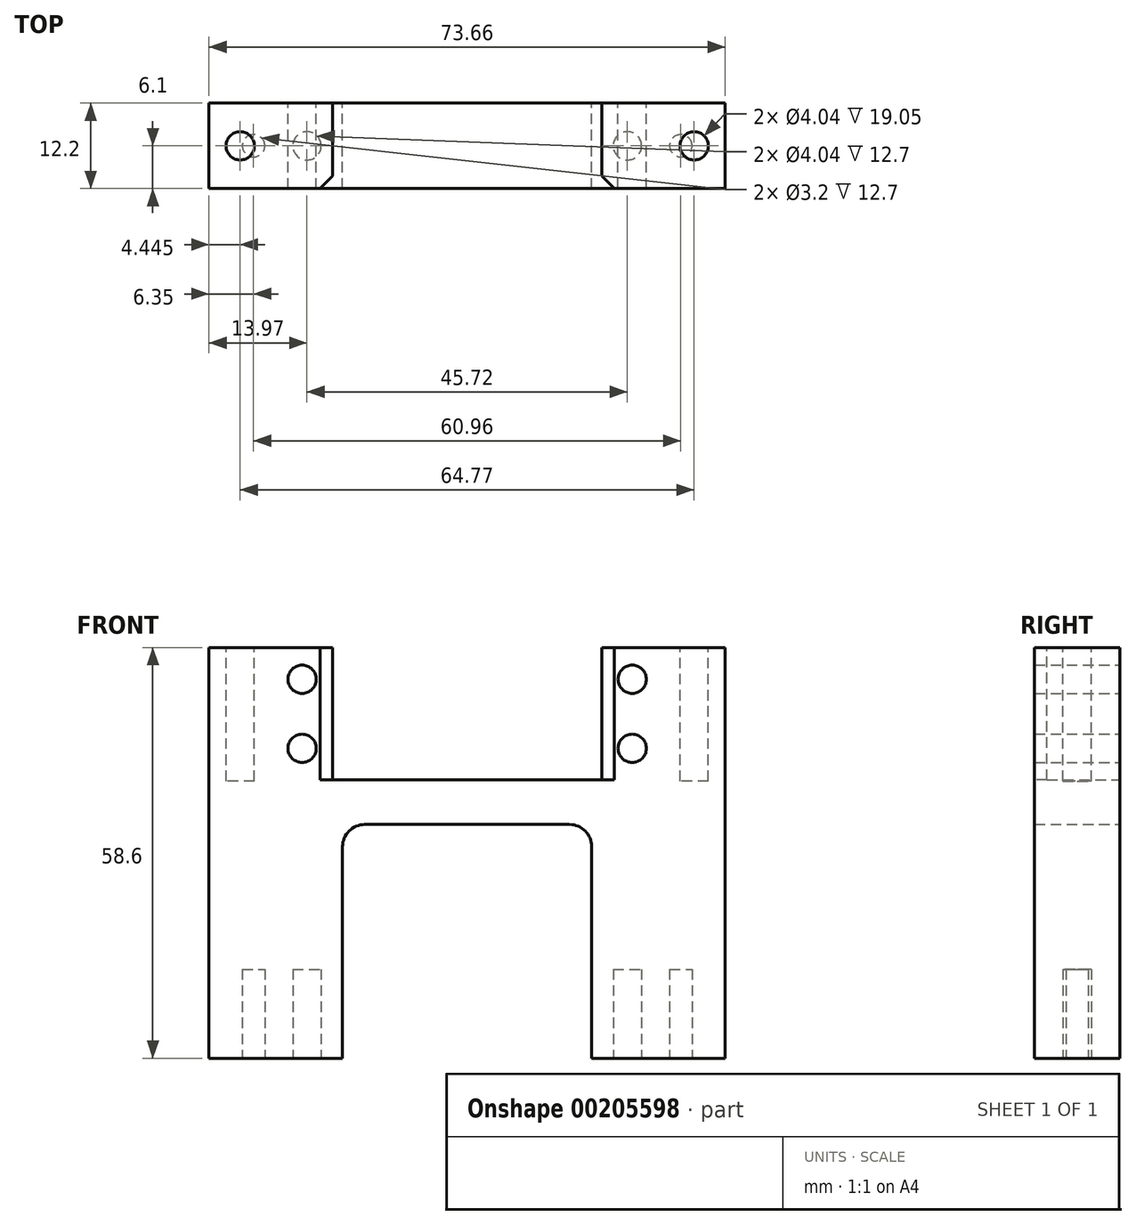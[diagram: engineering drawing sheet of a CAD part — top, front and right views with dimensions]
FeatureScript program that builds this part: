
annotation { "Feature Type Name" : "Feature", "Feature Type Description" : "" }
export const myFeature = defineFeature(function(context is Context, id is Id, definition is map)
    precondition{}
    {
        {
            var Q0;
            Q0=qCreatedBy(makeId("Front.planeOp"),FACE);
            var sketch = newSketch(context, id + "F0", { "sketchPlane" : qUnion([Q0])});
            skLineSegment(sketch, "E0", {"start": v(-36.83, 0) * mm, "end": v(-17.78, 0) * mm});
            skLineSegment(sketch, "E1", {"start": v(36.83, 0) * mm, "end": v(36.83, 58.6) * mm});
            skLineSegment(sketch, "E2", {"start": v(36.83, 58.6) * mm, "end": v(19.2, 58.6) * mm});
            skLineSegment(sketch, "E3", {"start": v(19.2, 58.6) * mm, "end": v(19.2, 39.7) * mm});
            skLineSegment(sketch, "E4", {"start": v(19.2, 39.7) * mm, "end": v(-19.2, 39.7) * mm});
            skLineSegment(sketch, "E5", {"start": v(-19.2, 39.7) * mm, "end": v(-19.2, 58.6) * mm});
            skLineSegment(sketch, "E6", {"start": v(-19.2, 58.6) * mm, "end": v(-36.83, 58.6) * mm});
            skLineSegment(sketch, "E7", {"start": v(-36.83, 58.6) * mm, "end": v(-36.83, 0) * mm});
            skCircle(sketch, "E8", {"center": v(-23.55, 54.08) * mm, "radius": 2.02 * mm});
            skCircle(sketch, "E9", {"center": v(-23.55, 44.22) * mm, "radius": 2.02 * mm});
            skCircle(sketch, "E10", {"center": v(23.55, 54.08) * mm, "radius": 2.02 * mm});
            skCircle(sketch, "E11", {"center": v(23.55, 44.22) * mm, "radius": 2.02 * mm});
            skLineSegment(sketch, "E12", {"start": v(-17.78, 0) * mm, "end": v(-17.78, 33.35) * mm});
            skLineSegment(sketch, "E13", {"start": v(-17.78, 33.35) * mm, "end": v(17.78, 33.35) * mm});
            skLineSegment(sketch, "E14", {"start": v(17.78, 33.35) * mm, "end": v(17.78, 0) * mm});
            skLineSegment(sketch, "E15.trimOffspring", {"start": v(17.78, 0) * mm, "end": v(36.83, 0) * mm});
            skSolve(sketch);
        }
        {
            var Q0;
            Q0=qSketchRegion(id+"F0",true);
            extrude(context, id + "F1", {"entities" : qUnion([Q0]), "flatOperationType" : FlatOperationType.REMOVE, "offsetDistance" : 25.4 * mm, "depth" : 12.2 * mm, "domain" : OperationDomain.MODEL, "symmetric" : true});
        }
        {
            var Q0;
            Q0=makeQuery(id+"F1.opExtrude","SWEPT_FACE",FACE,{"disambiguationData":[OSD([sQuery(id+"F0.wireOp",EDGE,"E6")])]});
            var sketch = newSketch(context, id + "F2", { "sketchPlane" : qUnion([Q0])});
            skCircle(sketch, "E16", {"center": v(-32.38, 0) * mm, "radius": 2.02 * mm});
            skCircle(sketch, "E17", {"center": v(32.39, 0) * mm, "radius": 2.02 * mm});
            skSolve(sketch);
        }
        {
            var Q0;
            Q0=qSketchRegion(id+"F2",true);
            extrude(context, id + "F3", {"entities" : qUnion([Q0]), "operationType" : NewBodyOperationType.REMOVE, "oppositeDirection" : true, "depth" : 19.05 * mm});
        }
        {
            var Q0;
            Q0=makeQuery(id+"F1.opExtrude","SWEPT_FACE",FACE,{"disambiguationData":[OSD([sQuery(id+"F0.wireOp",EDGE,"E0")])]});
            var sketch = newSketch(context, id + "F4", { "sketchPlane" : qUnion([Q0])});
            skCircle(sketch, "E18", {"center": v(30.48, 0) * mm, "radius": 1.6 * mm});
            skCircle(sketch, "E19", {"center": v(22.86, 0) * mm, "radius": 2.02 * mm});
            skCircle(sketch, "E20", {"center": v(-22.86, 0) * mm, "radius": 2.02 * mm});
            skCircle(sketch, "E21", {"center": v(-30.48, 0) * mm, "radius": 1.6 * mm});
            skSolve(sketch);
        }
        {
            var Q0;
            Q0=qSketchRegion(id+"F4",true);
            extrude(context, id + "F5", {"entities" : qUnion([Q0]), "operationType" : NewBodyOperationType.REMOVE, "oppositeDirection" : true, "depth" : 12.7 * mm});
        }
        {
            var Q0;
            Q0=makeQuery(id+"F1.opExtrude","CAP_EDGE",EDGE,{"disambiguationData":[OSD([sQuery(id+"F0.wireOp",EDGE,"E5")])],"isStart":false});
            var Q1;
            Q1=makeQuery(id+"F1.opExtrude","CAP_EDGE",EDGE,{"disambiguationData":[OSD([sQuery(id+"F0.wireOp",EDGE,"E3")])],"isStart":false});
            chamfer(context, id + "F6", {"entities" : qUnion([Q0, Q1]), "width" : 1.78 * mm, "tangentPropagation" : true});
        }
        {
            var Q0;
            Q0=makeQuery(id+"F1.opExtrude","SWEPT_EDGE",EDGE,{"disambiguationData":[OSD([sQuery(id+"F0.wireOp",EDGE,"E12"),sQuery(id+"F0.wireOp",EDGE,"E13")])]});
            var Q1;
            Q1=makeQuery(id+"F1.opExtrude","SWEPT_EDGE",EDGE,{"disambiguationData":[OSD([sQuery(id+"F0.wireOp",EDGE,"E13"),sQuery(id+"F0.wireOp",EDGE,"E14")])]});
            fillet(context, id + "F7", {"entities" : qUnion([Q0, Q1]), "radius" : 3.17 * mm, "tangentPropagation" : true, "allowEdgeOverflow" : false});
        }
    });
